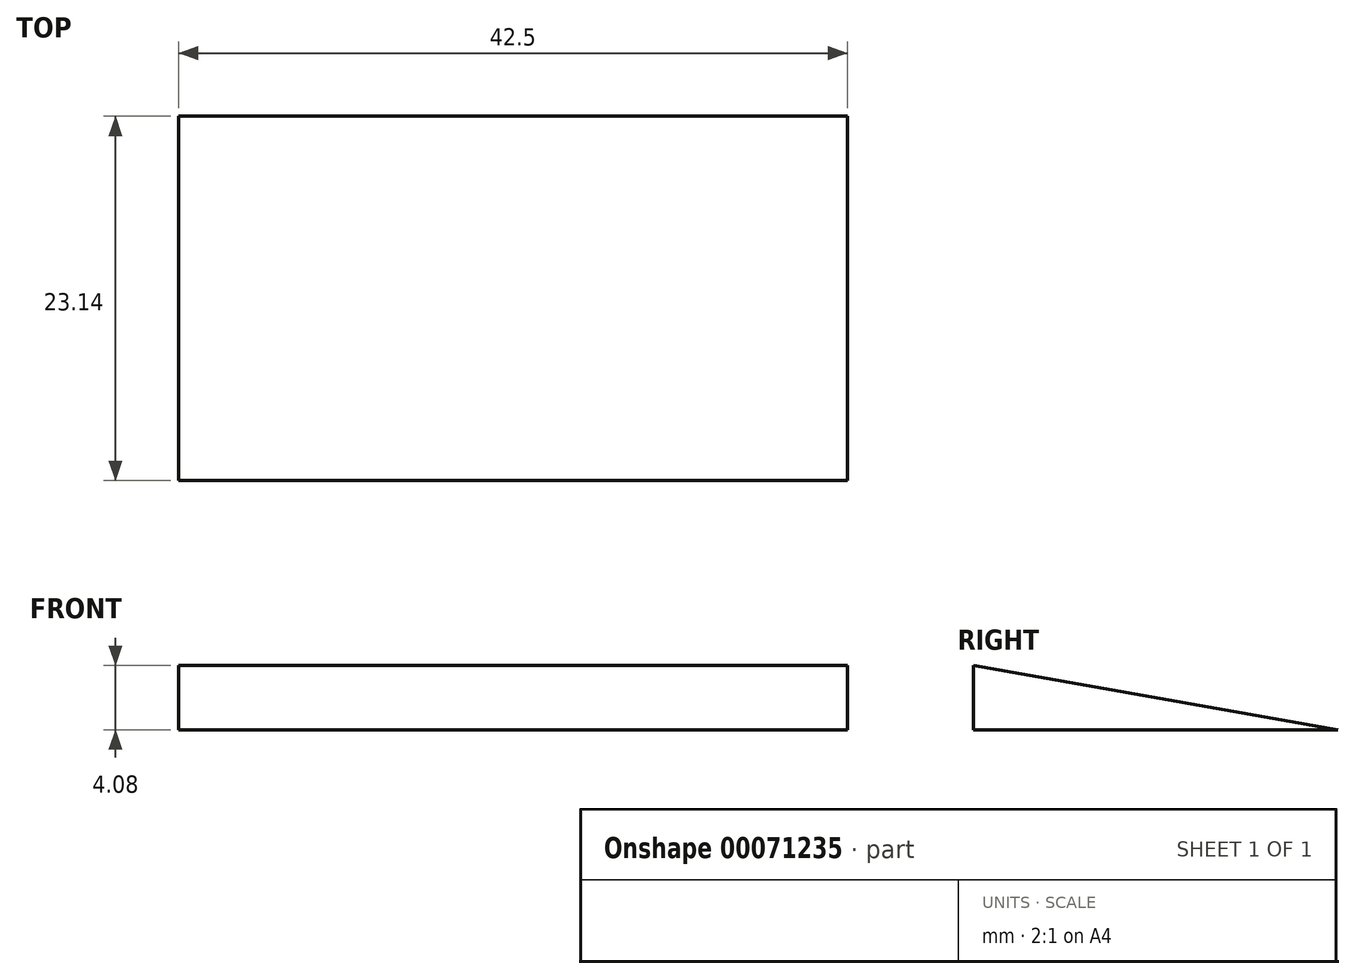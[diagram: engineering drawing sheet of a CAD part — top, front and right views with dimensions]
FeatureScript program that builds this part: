
annotation { "Feature Type Name" : "Feature", "Feature Type Description" : "" }
export const myFeature = defineFeature(function(context is Context, id is Id, definition is map)
    precondition{}
    {
        {
            var Q0;
            Q0=qCreatedBy(makeId("Right.planeOp"),FACE);
            var sketch = newSketch(context, id + "F0", { "sketchPlane" : qUnion([Q0])});
            skLineSegment(sketch, "E0", {"start": v(0, 4.08) * mm, "end": v(23.14, 0) * mm});
            skLineSegment(sketch, "E1", {"start": v(23.14, 0) * mm, "end": v(0, 0) * mm});
            skLineSegment(sketch, "E2", {"start": v(0, 4.08) * mm, "end": v(0, 0) * mm});
            skSolve(sketch);
        }
        {
            var Q0;
            Q0 = qSketchRegion(id + "F0", true);
            extrude(context, id + "F1", {"entities" : qUnion([Q0]), "depth" : 42.5 * mm});
        }
    });
